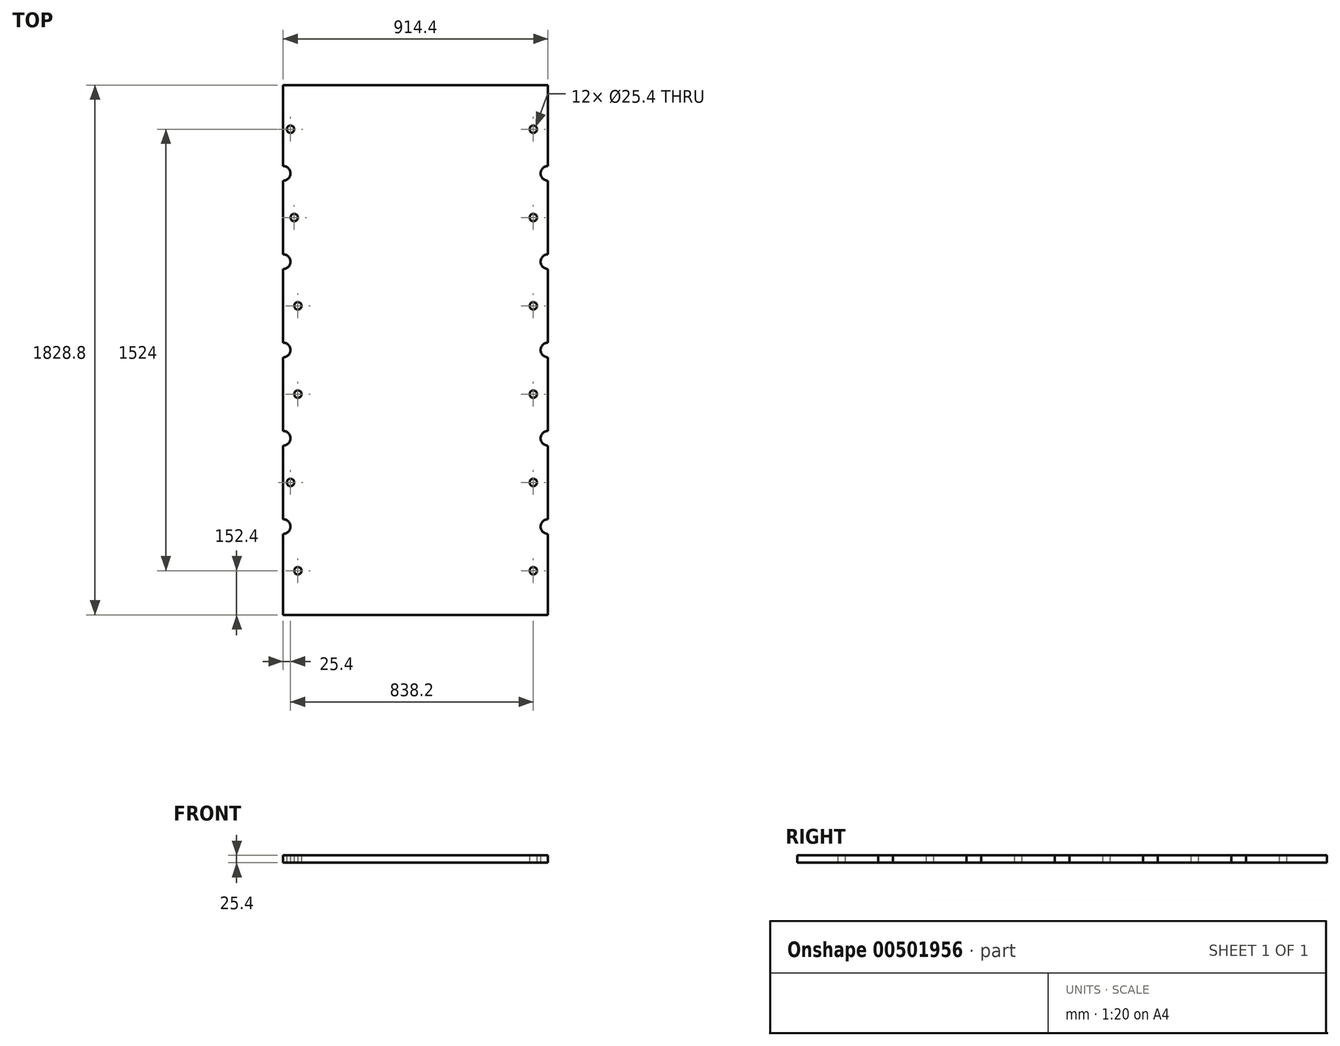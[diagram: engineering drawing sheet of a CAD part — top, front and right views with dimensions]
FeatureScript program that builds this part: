
annotation { "Feature Type Name" : "Feature", "Feature Type Description" : "" }
export const myFeature = defineFeature(function(context is Context, id is Id, definition is map)
    precondition{}
    {
        {
            var Q0;
            Q0=qCreatedBy(makeId("Top.planeOp"),FACE);
            var sketch = newSketch(context, id + "F0", { "sketchPlane" : qUnion([Q0])});
            skLineSegment(sketch, "E0.bottom", {"start": v(457.2, -914.4) * mm, "end": v(-457.2, -914.4) * mm});
            skLineSegment(sketch, "E0.top", {"start": v(457.2, 914.4) * mm, "end": v(-457.2, 914.4) * mm});
            skLineSegment(sketch, "E0.left", {"start": v(457.2, -914.4) * mm, "end": v(457.2, -635) * mm});
            skLineSegment(sketch, "E0.right", {"start": v(-457.2, -914.4) * mm, "end": v(-457.2, -635) * mm});
            skPoint(sketch, "E0.middle", {"position": v(0, 0) * mm});
            skArc(sketch, "E1", {"start": v(-457.2, -25.4) * mm, "mid": v(-431.8, 0) * mm, "end": v(-457.2, 25.4) * mm});
            skArc(sketch, "E2", {"start": v(-457.2, 279.4) * mm, "mid": v(-431.8, 304.8) * mm, "end": v(-457.2, 330.2) * mm});
            skArc(sketch, "E3", {"start": v(-457.2, -330.2) * mm, "mid": v(-431.8, -304.8) * mm, "end": v(-457.2, -279.4) * mm});
            skArc(sketch, "E4", {"start": v(-457.2, 584.2) * mm, "mid": v(-431.8, 609.6) * mm, "end": v(-457.2, 635) * mm});
            skArc(sketch, "E5", {"start": v(-457.2, -635) * mm, "mid": v(-431.8, -609.6) * mm, "end": v(-457.2, -584.2) * mm});
            skLineSegment(sketch, "E6.trimOffspring", {"start": v(-457.2, 635) * mm, "end": v(-457.2, 914.4) * mm});
            skLineSegment(sketch, "E7.trimOffspring", {"start": v(-457.2, 330.2) * mm, "end": v(-457.2, 584.2) * mm});
            skLineSegment(sketch, "E8.trimOffspring", {"start": v(-457.2, 25.4) * mm, "end": v(-457.2, 279.4) * mm});
            skLineSegment(sketch, "E9.trimOffspring", {"start": v(-457.2, -279.4) * mm, "end": v(-457.2, -25.4) * mm});
            skLineSegment(sketch, "E10.trimOffspring", {"start": v(-457.2, -584.2) * mm, "end": v(-457.2, -330.2) * mm});
            skArc(sketch, "E11", {"start": v(457.2, 25.4) * mm, "mid": v(431.8, 0) * mm, "end": v(457.2, -25.4) * mm});
            skArc(sketch, "E12", {"start": v(457.2, 330.2) * mm, "mid": v(431.8, 304.8) * mm, "end": v(457.2, 279.4) * mm});
            skArc(sketch, "E13", {"start": v(457.2, 635) * mm, "mid": v(431.8, 609.6) * mm, "end": v(457.2, 584.2) * mm});
            skArc(sketch, "E14", {"start": v(457.2, -279.4) * mm, "mid": v(431.8, -304.8) * mm, "end": v(457.2, -330.2) * mm});
            skArc(sketch, "E15", {"start": v(457.2, -584.2) * mm, "mid": v(431.8, -609.6) * mm, "end": v(457.2, -635) * mm});
            skLineSegment(sketch, "E16.trimOffspring", {"start": v(457.2, -584.2) * mm, "end": v(457.2, -330.2) * mm});
            skLineSegment(sketch, "E17.trimOffspring", {"start": v(457.2, -279.4) * mm, "end": v(457.2, -25.4) * mm});
            skLineSegment(sketch, "E18.trimOffspring", {"start": v(457.2, 25.4) * mm, "end": v(457.2, 279.4) * mm});
            skLineSegment(sketch, "E19.trimOffspring", {"start": v(457.2, 330.2) * mm, "end": v(457.2, 584.2) * mm});
            skLineSegment(sketch, "E20.trimOffspring", {"start": v(457.2, 635) * mm, "end": v(457.2, 914.4) * mm});
            skCircle(sketch, "E21", {"center": v(-419.1, 457.2) * mm, "radius": 12.7 * mm});
            skCircle(sketch, "E22", {"center": v(-431.8, 762) * mm, "radius": 12.7 * mm});
            skCircle(sketch, "E23", {"center": v(-406.4, 152.4) * mm, "radius": 12.7 * mm});
            skCircle(sketch, "E24", {"center": v(-406.4, -152.4) * mm, "radius": 12.7 * mm});
            skCircle(sketch, "E25", {"center": v(-431.8, -457.2) * mm, "radius": 12.7 * mm});
            skCircle(sketch, "E26", {"center": v(-406.4, -762) * mm, "radius": 12.7 * mm});
            skCircle(sketch, "E27", {"center": v(406.4, -762) * mm, "radius": 12.7 * mm});
            skCircle(sketch, "E28", {"center": v(406.4, -457.2) * mm, "radius": 12.7 * mm});
            skCircle(sketch, "E29", {"center": v(406.4, -152.4) * mm, "radius": 12.7 * mm});
            skCircle(sketch, "E30", {"center": v(406.4, 152.4) * mm, "radius": 12.7 * mm});
            skCircle(sketch, "E31", {"center": v(406.4, 762) * mm, "radius": 12.7 * mm});
            skPoint(sketch, "E32.end.orphan", {"position": v(457.2, 838.2) * mm});
            skCircle(sketch, "E33", {"center": v(406.4, 457.2) * mm, "radius": 12.7 * mm});
            skPoint(sketch, "E34.end.orphan", {"position": v(457.2, -838.2) * mm});
            skSolve(sketch);
        }
        {
            var Q0;
            Q0 = qSketchRegion(id + "F0", true);
            var Q1;
            Q1 = qSketchRegion(id + "F0", true);
            extrude(context, id + "F1", {"entities" : qUnion([Q0, Q1]), "depth" : 25.4 * mm});
        }
    });
